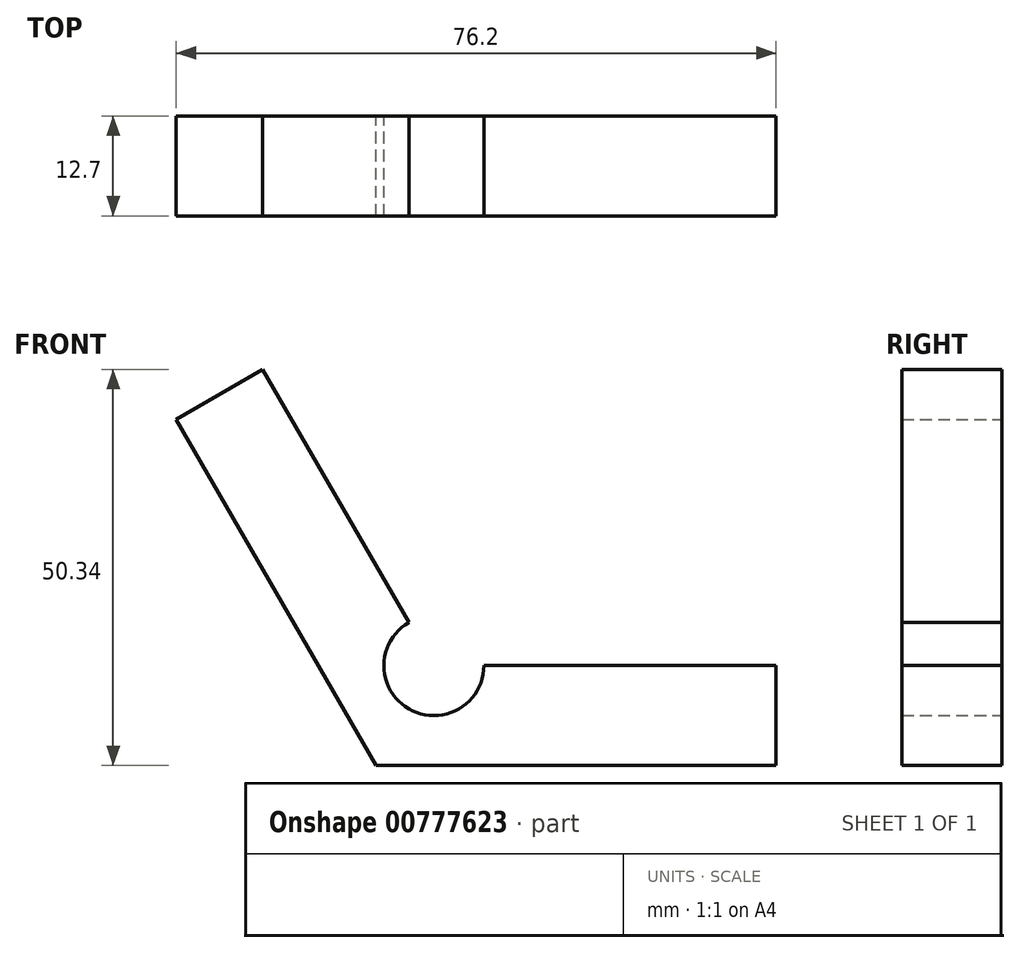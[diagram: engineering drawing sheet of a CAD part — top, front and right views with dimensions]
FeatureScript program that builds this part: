
annotation { "Feature Type Name" : "Feature", "Feature Type Description" : "" }
export const myFeature = defineFeature(function(context is Context, id is Id, definition is map)
    precondition{}
    {
        {
            var Q0;
            Q0=qCreatedBy(makeId("Front.planeOp"),FACE);
            var sketch = newSketch(context, id + "F0", { "sketchPlane" : qUnion([Q0])});
            skLineSegment(sketch, "E0", {"start": v(0, 0) * mm, "end": v(50.8, 0) * mm});
            skLineSegment(sketch, "E1", {"start": v(0, 0) * mm, "end": v(-25.4, 44) * mm});
            skLineSegment(sketch, "E2.0", {"start": v(4.16, 18.2) * mm, "end": v(-14.4, 50.34) * mm});
            skLineSegment(sketch, "E3.0", {"start": v(13.68, 12.7) * mm, "end": v(50.8, 12.7) * mm});
            skLineSegment(sketch, "E4", {"start": v(50.8, 0) * mm, "end": v(50.8, 12.7) * mm});
            skLineSegment(sketch, "E5", {"start": v(-25.4, 44) * mm, "end": v(-14.4, 50.34) * mm});
            skArc(sketch, "E6", {"start": v(4.16, 18.2) * mm, "mid": v(4.16, 7.2) * mm, "end": v(13.68, 12.7) * mm});
            skSolve(sketch);
        }
        {
            var Q0;
            Q0=makeQuery(id+"F0.imprint","IMPRINT",FACE,{"disambiguationData":[TD([[makeQuery(id+"F0.imprint","IMPRINT",EDGE,{"derivedFrom":sQuery(id+"F0.wireOp",EDGE,"E0")}),1.0]])]});
            extrude(context, id + "F1", {"entities" : qUnion([Q0]), "depth" : 12.7 * mm, "offsetDistance" : 25.4 * mm});
        }
    });
